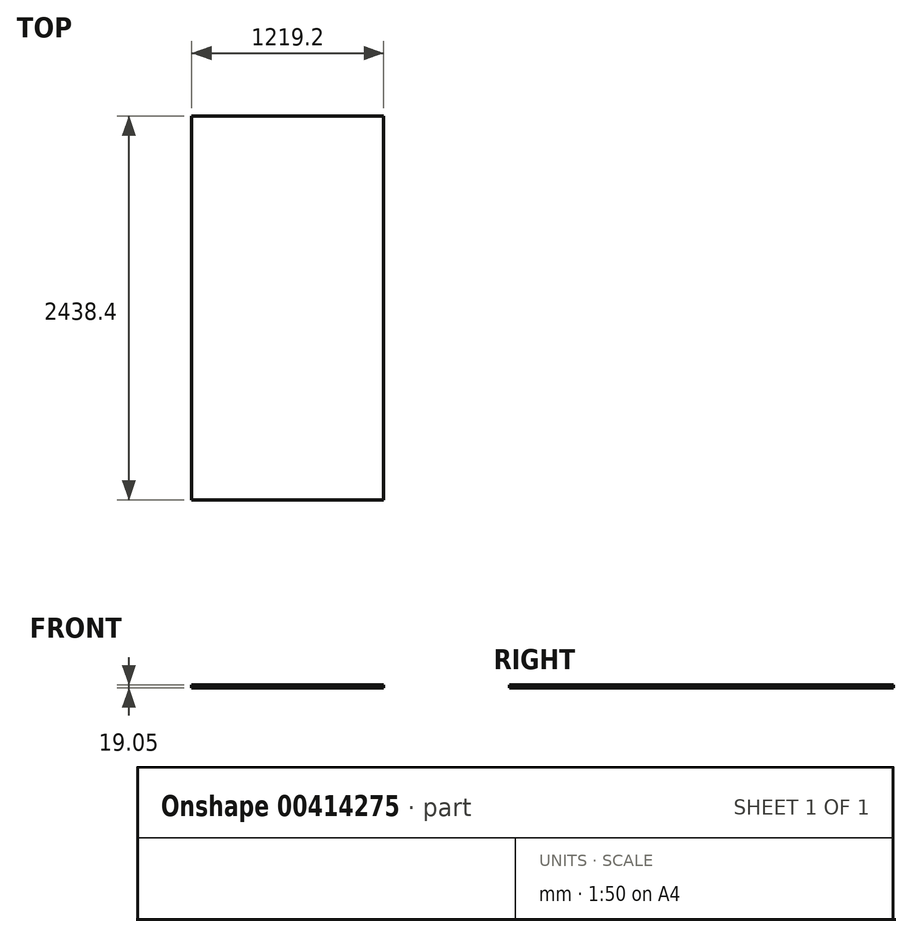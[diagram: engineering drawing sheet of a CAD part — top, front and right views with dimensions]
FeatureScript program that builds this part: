
annotation { "Feature Type Name" : "Feature", "Feature Type Description" : "" }
export const myFeature = defineFeature(function(context is Context, id is Id, definition is map)
    precondition{}
    {
        {
            var Q0;
            Q0=qCreatedBy(makeId("Top.planeOp"),FACE);
            var sketch = newSketch(context, id + "F0", { "sketchPlane" : qUnion([Q0])});
            skLineSegment(sketch, "E0.bottom", {"start": v(-606.16, 1561.27) * mm, "end": v(613.04, 1561.27) * mm});
            skLineSegment(sketch, "E0.top", {"start": v(-606.16, -877.13) * mm, "end": v(613.04, -877.13) * mm});
            skLineSegment(sketch, "E0.left", {"start": v(-606.16, 1561.27) * mm, "end": v(-606.16, -877.13) * mm});
            skLineSegment(sketch, "E0.right", {"start": v(613.04, 1561.27) * mm, "end": v(613.04, -877.13) * mm});
            skSolve(sketch);
        }
        {
            var Q0;
            Q0=makeQuery(id+"F0.imprint","IMPRINT",FACE,{"disambiguationData":[TD([[makeQuery(id+"F0.imprint","IMPRINT",EDGE,{"derivedFrom":sQuery(id+"F0.wireOp",EDGE,"E0.bottom")}),-1.0]])]});
            extrude(context, id + "F1", {"entities" : qUnion([Q0]), "depth" : 19.05 * mm});
        }
    });
